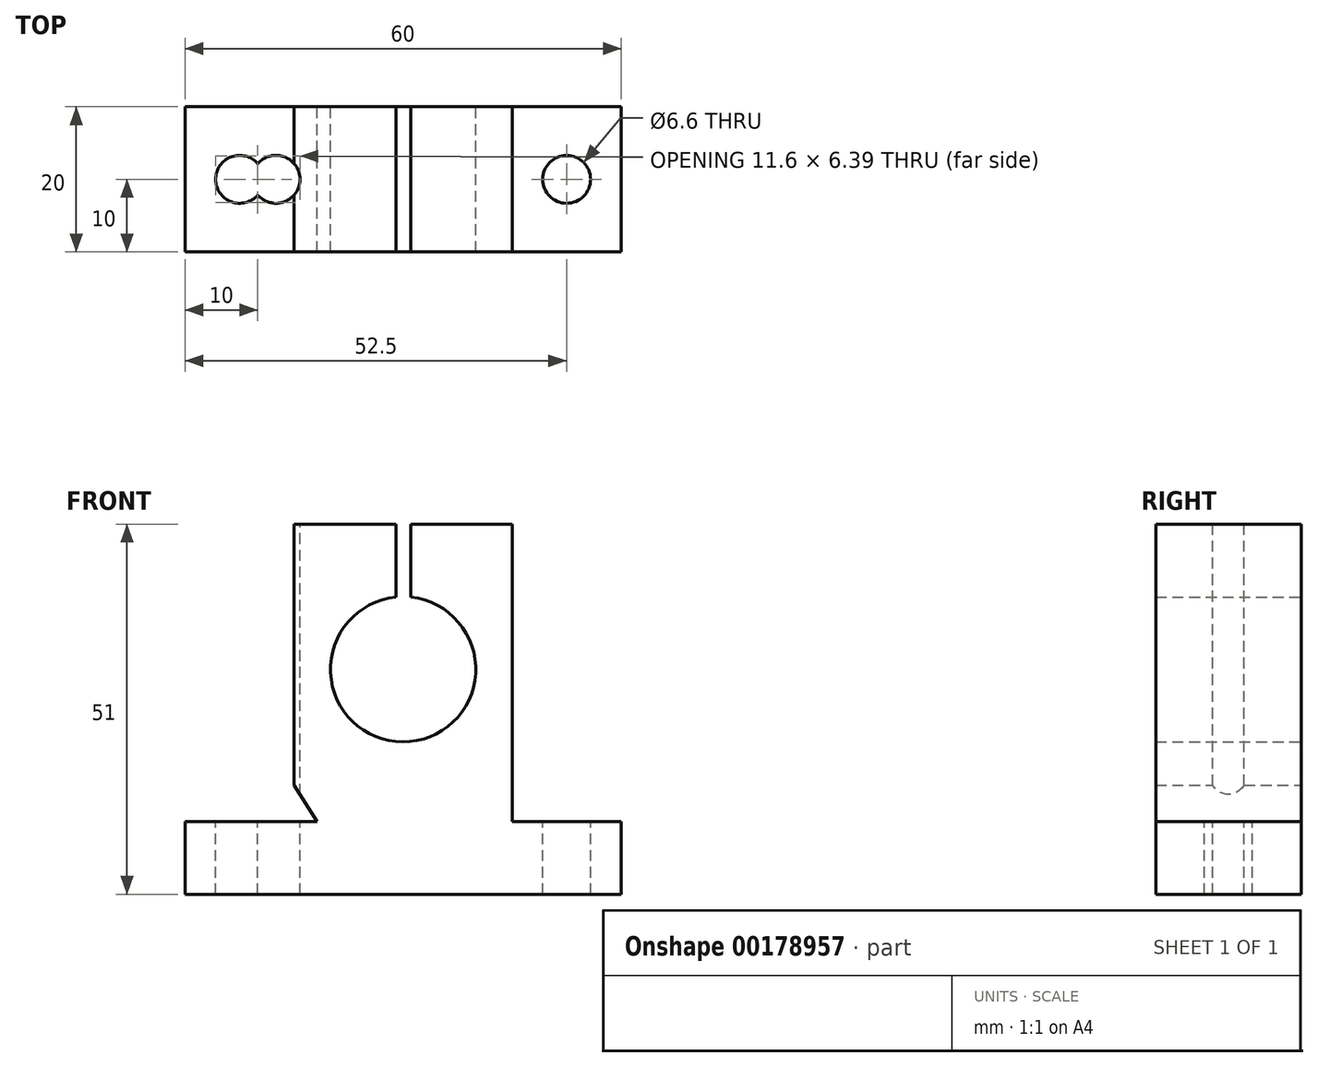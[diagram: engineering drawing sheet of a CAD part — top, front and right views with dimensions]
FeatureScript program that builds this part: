
annotation { "Feature Type Name" : "Feature", "Feature Type Description" : "" }
export const myFeature = defineFeature(function(context is Context, id is Id, definition is map)
    precondition{}
    {
        {
            var Q0;
            Q0=qCreatedBy(makeId("Front.planeOp"),FACE);
            var sketch = newSketch(context, id + "F0", { "sketchPlane" : qUnion([Q0])});
            skLineSegment(sketch, "E0.bottom", {"start": v(30, -25.5) * mm, "end": v(-30, -25.5) * mm});
            skLineSegment(sketch, "E0.top", {"start": v(15, 25.5) * mm, "end": v(1.06, 25.5) * mm});
            skLineSegment(sketch, "E0.left", {"start": v(30, -25.5) * mm, "end": v(30, -15.5) * mm});
            skLineSegment(sketch, "E0.right", {"start": v(-30, -25.5) * mm, "end": v(-30, -15.5) * mm});
            skPoint(sketch, "E0.middle", {"position": v(0, 0) * mm});
            skLineSegment(sketch, "E1", {"start": v(-15, 25.5) * mm, "end": v(-15, -10.49) * mm});
            skLineSegment(sketch, "E2", {"start": v(15, 25.5) * mm, "end": v(15, -15.5) * mm});
            skLineSegment(sketch, "E3", {"start": v(-30, -15.5) * mm, "end": v(-15, -15.5) * mm});
            skArc(sketch, "E4", {"start": v(-0.95, 15.45) * mm, "mid": v(-0.05, -4.5) * mm, "end": v(1.06, 15.44) * mm});
            skLineSegment(sketch, "E5", {"start": v(-0.95, 25.5) * mm, "end": v(-0.95, 15.45) * mm});
            skLineSegment(sketch, "E6", {"start": v(1.06, 25.5) * mm, "end": v(1.06, 15.44) * mm});
            skPoint(sketch, "E7.orphan", {"position": v(-30, 25.5) * mm});
            skLineSegment(sketch, "E8.trimOffspring", {"start": v(-0.95, 25.5) * mm, "end": v(-15, 25.5) * mm});
            skPoint(sketch, "E9.orphan", {"position": v(30, 25.5) * mm});
            skPoint(sketch, "E10.orphan", {"position": v(30, 5.5) * mm});
            skPoint(sketch, "E11.orphan", {"position": v(-30, 5.5) * mm});
            skLineSegment(sketch, "E12.trimOffspring", {"start": v(15, -15.5) * mm, "end": v(30, -15.5) * mm});
            skLineSegment(sketch, "E13", {"start": v(-15, -15.5) * mm, "end": v(-11.82, -15.5) * mm});
            skLineSegment(sketch, "E14", {"start": v(-11.82, -15.5) * mm, "end": v(-15, -10.49) * mm});
            skSolve(sketch);
        }
        {
            var Q0;
            Q0=makeQuery(id+"F0.imprint","IMPRINT",FACE,{"disambiguationData":[TD([[makeQuery(id+"F0.imprint","IMPRINT",EDGE,{"derivedFrom":sQuery(id+"F0.wireOp",EDGE,"E0.bottom")}),-1.0]])]});
            extrude(context, id + "F1", {"entities" : qUnion([Q0]), "depth" : 20 * mm});
        }
        {
            var Q0;
            Q0=makeQuery(id+"F1.opExtrude","SWEPT_FACE",FACE,{"disambiguationData":[OSD([sQuery(id+"F0.wireOp",EDGE,"E0.bottom")])]});
            var sketch = newSketch(context, id + "F2", { "sketchPlane" : qUnion([Q0])});
            skArc(sketch, "E15", {"start": v(-20, 12.15) * mm, "mid": v(-25.8, 10) * mm, "end": v(-20, 7.85) * mm});
            skCircle(sketch, "E16", {"center": v(22.5, 10) * mm, "radius": 3.3 * mm});
            skPoint(sketch, "E17.orphan", {"position": v(-22.5, 20) * mm});
            skPoint(sketch, "E18.orphan", {"position": v(-30, 10) * mm});
            skPoint(sketch, "E19.orphan", {"position": v(-22.5, 0) * mm});
            skPoint(sketch, "E20.orphan", {"position": v(22.5, 0) * mm});
            skPoint(sketch, "E21.orphan", {"position": v(30, 10) * mm});
            skPoint(sketch, "E22.orphan", {"position": v(22.5, 20) * mm});
            skArc(sketch, "E23", {"start": v(-20, 7.85) * mm, "mid": v(-14.2, 10) * mm, "end": v(-20, 12.15) * mm});
            skPoint(sketch, "E24.orphan", {"position": v(-17.5, 20) * mm});
            skPoint(sketch, "E25.start.orphan", {"position": v(-17.5, 0) * mm});
            skSolve(sketch);
        }
        {
            var Q0;
            Q0=sQuery(id+"F2.wireOp",VERTEX,"E15.center");
            var Q1;
            Q1=makeQuery(id+"F1.opExtrude","SWEPT_BODY",BODY,{"disambiguationData":[OSD([sQuery(id+"F0.wireOp",EDGE,"E0.bottom"),sQuery(id+"F0.wireOp",EDGE,"E0.top"),sQuery(id+"F0.wireOp",EDGE,"E0.left"),sQuery(id+"F0.wireOp",EDGE,"E0.right"),sQuery(id+"F0.wireOp",EDGE,"E1"),sQuery(id+"F0.wireOp",EDGE,"E2"),sQuery(id+"F0.wireOp",EDGE,"E3"),sQuery(id+"F0.wireOp",EDGE,"E4"),sQuery(id+"F0.wireOp",EDGE,"E5"),sQuery(id+"F0.wireOp",EDGE,"E6"),sQuery(id+"F0.wireOp",EDGE,"E8.trimOffspring"),sQuery(id+"F0.wireOp",EDGE,"E12.trimOffspring")])]});
            hole(context, id + "F3", {"style" : HoleStyle.SIMPLE, "endStyle" : HoleEndStyle.THROUGH, "holeDiameter" : 6.6 * mm, "locations" : qUnion([Q0]), "scope" : qUnion([Q1]), "isTappedThrough" : true});
        }
        {
            var Q0;
            Q0=sQuery(id+"F2.wireOp",VERTEX,"E16.center");
            var Q1;
            Q1=makeQuery(id+"F1.opExtrude","SWEPT_BODY",BODY,{"disambiguationData":[OSD([sQuery(id+"F0.wireOp",EDGE,"E0.bottom"),sQuery(id+"F0.wireOp",EDGE,"E0.top"),sQuery(id+"F0.wireOp",EDGE,"E0.left"),sQuery(id+"F0.wireOp",EDGE,"E0.right"),sQuery(id+"F0.wireOp",EDGE,"E1"),sQuery(id+"F0.wireOp",EDGE,"E2"),sQuery(id+"F0.wireOp",EDGE,"E3"),sQuery(id+"F0.wireOp",EDGE,"E4"),sQuery(id+"F0.wireOp",EDGE,"E5"),sQuery(id+"F0.wireOp",EDGE,"E6"),sQuery(id+"F0.wireOp",EDGE,"E8.trimOffspring"),sQuery(id+"F0.wireOp",EDGE,"E12.trimOffspring")])]});
            hole(context, id + "F4", {"style" : HoleStyle.SIMPLE, "endStyle" : HoleEndStyle.THROUGH, "holeDiameter" : 6.6 * mm, "locations" : qUnion([Q0]), "scope" : qUnion([Q1]), "isTappedThrough" : true});
        }
        {
            var Q0;
            Q0=sQuery(id+"F2.wireOp",VERTEX,"E23.center");
            var Q1;
            Q1=makeQuery(id+"F1.opExtrude","SWEPT_BODY",BODY,{"disambiguationData":[OSD([sQuery(id+"F0.wireOp",EDGE,"E0.bottom"),sQuery(id+"F0.wireOp",EDGE,"E0.top"),sQuery(id+"F0.wireOp",EDGE,"E0.left"),sQuery(id+"F0.wireOp",EDGE,"E0.right"),sQuery(id+"F0.wireOp",EDGE,"E1"),sQuery(id+"F0.wireOp",EDGE,"E2"),sQuery(id+"F0.wireOp",EDGE,"E3"),sQuery(id+"F0.wireOp",EDGE,"E4"),sQuery(id+"F0.wireOp",EDGE,"E5"),sQuery(id+"F0.wireOp",EDGE,"E6"),sQuery(id+"F0.wireOp",EDGE,"E8.trimOffspring"),sQuery(id+"F0.wireOp",EDGE,"E12.trimOffspring")])]});
            hole(context, id + "F5", {"style" : HoleStyle.SIMPLE, "endStyle" : HoleEndStyle.THROUGH, "holeDiameter" : 6.6 * mm, "locations" : qUnion([Q0]), "scope" : qUnion([Q1]), "isTappedThrough" : true});
        }
    });
